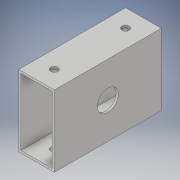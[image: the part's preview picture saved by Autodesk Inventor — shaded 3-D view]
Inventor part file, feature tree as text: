
AUTODESK INVENTOR PART (.ipt)
format: ipt  version: 2018 (Build 220112000, 112)  size: 123,392 bytes
history: native  units: in
note: dims shown in document units (in); Inventor stores cm internally (conversion verified against a paired STEP export)
features: extrude x3, sketch x3
ambient origin geometry x8: Origin, YZ Plane, XZ Plane, XY Plane, X Axis, Y Axis, Z Axis, Center Point
bodies: Solid1 (feature_tree)
feature tree (6):
  extrude  "Extrusion1"  Depth=2.0in
  extrude  "Extrusion3"  Depth=3.0in TaperAngle=0.0deg
  extrude  "Extrusion4"  Depth=1.0in TaperAngle=0.0deg
  sketch  "Sketch1"  dims[d0=1.0in d1=2.0in]
  sketch  "Sketch3"  dims[d2=0.0625in d3=3.0in d4=0.0in]
  sketch  "Sketch4"  dims[d10=1.0in d12=3.25in d13=0.0in d15=0.59in d16=0.5in d17=0.5in d18=0.2031in d19=3.25in d20=0.0in]
